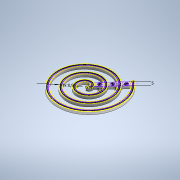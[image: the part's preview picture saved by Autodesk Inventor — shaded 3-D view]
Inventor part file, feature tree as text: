
AUTODESK INVENTOR PART (.ipt)
format: ipt  version: 2022.2 (Build 262287000, 287)  size: 776,704 bytes
history: native  units: mm
features: other x4, extrude x3, sketch x1, fillet x1, projected_geometry x1
ambient origin geometry x8: Origin, YZ Plane, XZ Plane, XY Plane, X Axis, Y Axis, Z Axis, Center Point
bodies: Body1 (feature_tree)
feature tree (10):
  other  "Rotor Wrap"
  extrude  "Rotor Wrap Extrusion"  Depth=5.0mm
  sketch  "Sketch7"  dims[d0=0.0mm d1=213.1131mm d2=100.0mm d3=100.0mm d4=119.751226mm d5=128.93306mm d8=0.0mm d9=181.697174mm d10=117.865222mm d11=126.600039mm d22=3.0mm d23=0.0mm d24=104.0mm d27=4.0mm d28=100.0mm d195=0.0mm d46=181.697174mm d50=0.0mm d51=213.1131mm d72=100.0mm d73=100.0mm d74=78.951679mm d78=98.0mm d79=100.0mm d82=73.06694mm d83=104.0mm d84=96.816901mm d87=1.5mm d98=5.844343mm d99=1.844343mm d100=9.746017mm d101=0.0mm d253=0.0mm d254=4.0mm d258=0.8mm d259=0.0mm d265=1.0mm d266=0.5mm d267=0.3mm d45=1.844343mm d47=5.844343mm d52=0.95mm d53=1.0mm d54=1.0mm d55=0.0mm d56=0.45mm d58=3.2mm d59=3.2mm d60=3.2mm d61=5.0mm d62=1.0mm d63=0.0mm]
  extrude  "Extrusion5"  Depth=5.0mm
  fillet  "Fillet2"  Radius=100.0mm
  extrude  "Extrusion6"  Depth=5.0mm
  other  "Rotor Profile"
  other  "rotor_outer"
  other  "rotor_inner"
  projected_geometry  "Projected Loop3"
